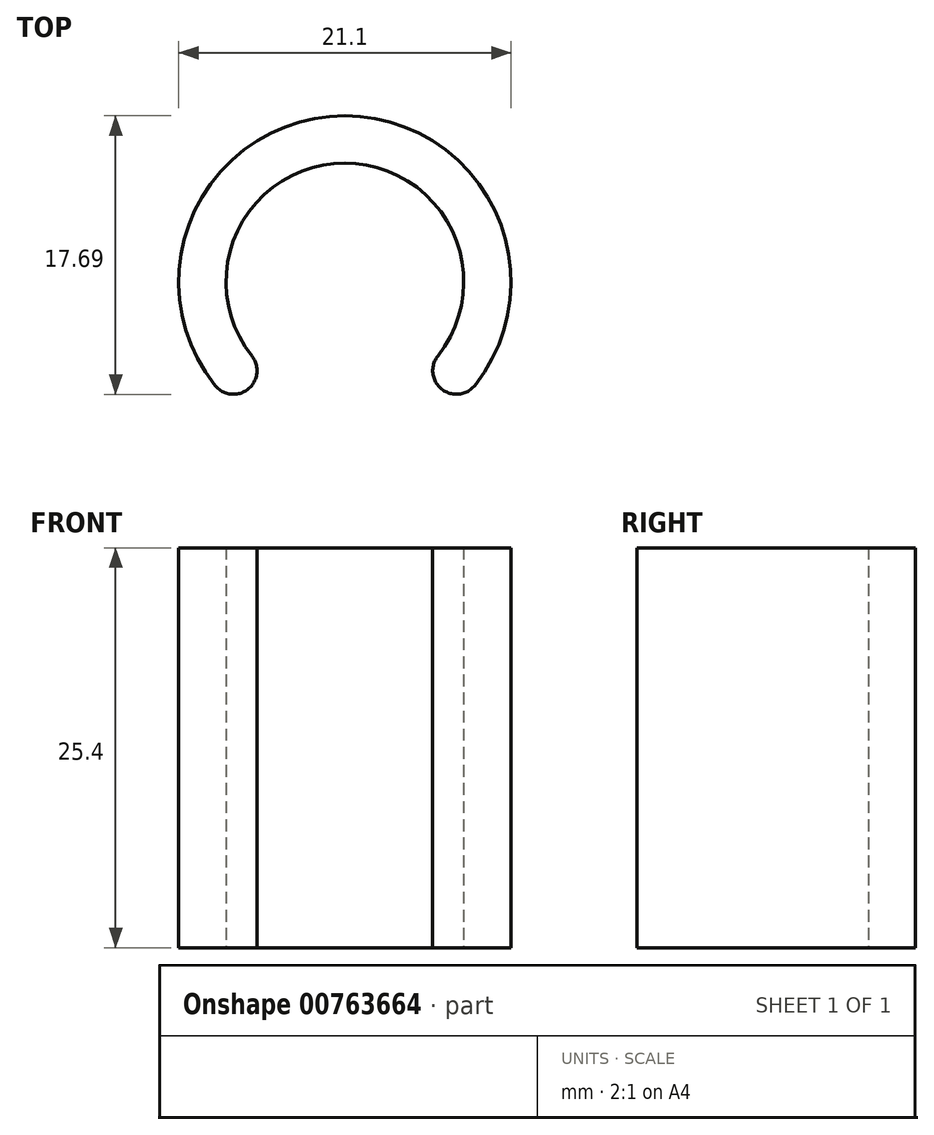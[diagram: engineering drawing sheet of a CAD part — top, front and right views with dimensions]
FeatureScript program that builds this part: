
annotation { "Feature Type Name" : "Feature", "Feature Type Description" : "" }
export const myFeature = defineFeature(function(context is Context, id is Id, definition is map)
    precondition{}
    {
        {
            var Q0;
            Q0=qCreatedBy(makeId("Top.planeOp"),FACE);
            var sketch = newSketch(context, id + "F0", { "sketchPlane" : qUnion([Q0])});
            skArc(sketch, "E0", {"start": v(0, 10.55) * mm, "mid": v(-9.5, 4.58) * mm, "end": v(-8.26, -6.57) * mm});
            skLineSegment(sketch, "E1", {"start": v(0, 10.55) * mm, "end": v(0, 0) * mm, "construction": true});
            skLineSegment(sketch, "E2", {"start": v(0, -6.57) * mm, "end": v(0, 0) * mm, "construction": true});
            skArc(sketch, "E3", {"start": v(0, 7.55) * mm, "mid": v(-6.8, 3.28) * mm, "end": v(-5.9, -4.7) * mm});
            skArc(sketch, "E4", {"start": v(-8.26, -6.57) * mm, "mid": v(-6.15, -6.8) * mm, "end": v(-5.9, -4.7) * mm});
            skLineSegment(sketch, "E5", {"start": v(-8.26, -6.57) * mm, "end": v(0, -6.57) * mm, "construction": true});
            skArc(sketch, "E6.MirrorCS", {"start": v(8.26, -6.57) * mm, "mid": v(6.15, -6.8) * mm, "end": v(5.9, -4.7) * mm});
            skArc(sketch, "E7.MirrorCS", {"start": v(0, 7.55) * mm, "mid": v(6.8, 3.28) * mm, "end": v(5.9, -4.7) * mm});
            skArc(sketch, "E8.MirrorCS", {"start": v(0, 10.55) * mm, "mid": v(9.5, 4.58) * mm, "end": v(8.26, -6.57) * mm});
            skSolve(sketch);
        }
        {
            var Q0;
            Q0 = qSketchRegion(id + "F0", true);
            extrude(context, id + "F1", {"entities" : qUnion([Q0]), "depth" : 25.4 * mm, "offsetDistance" : 25.4 * mm});
        }
    });
